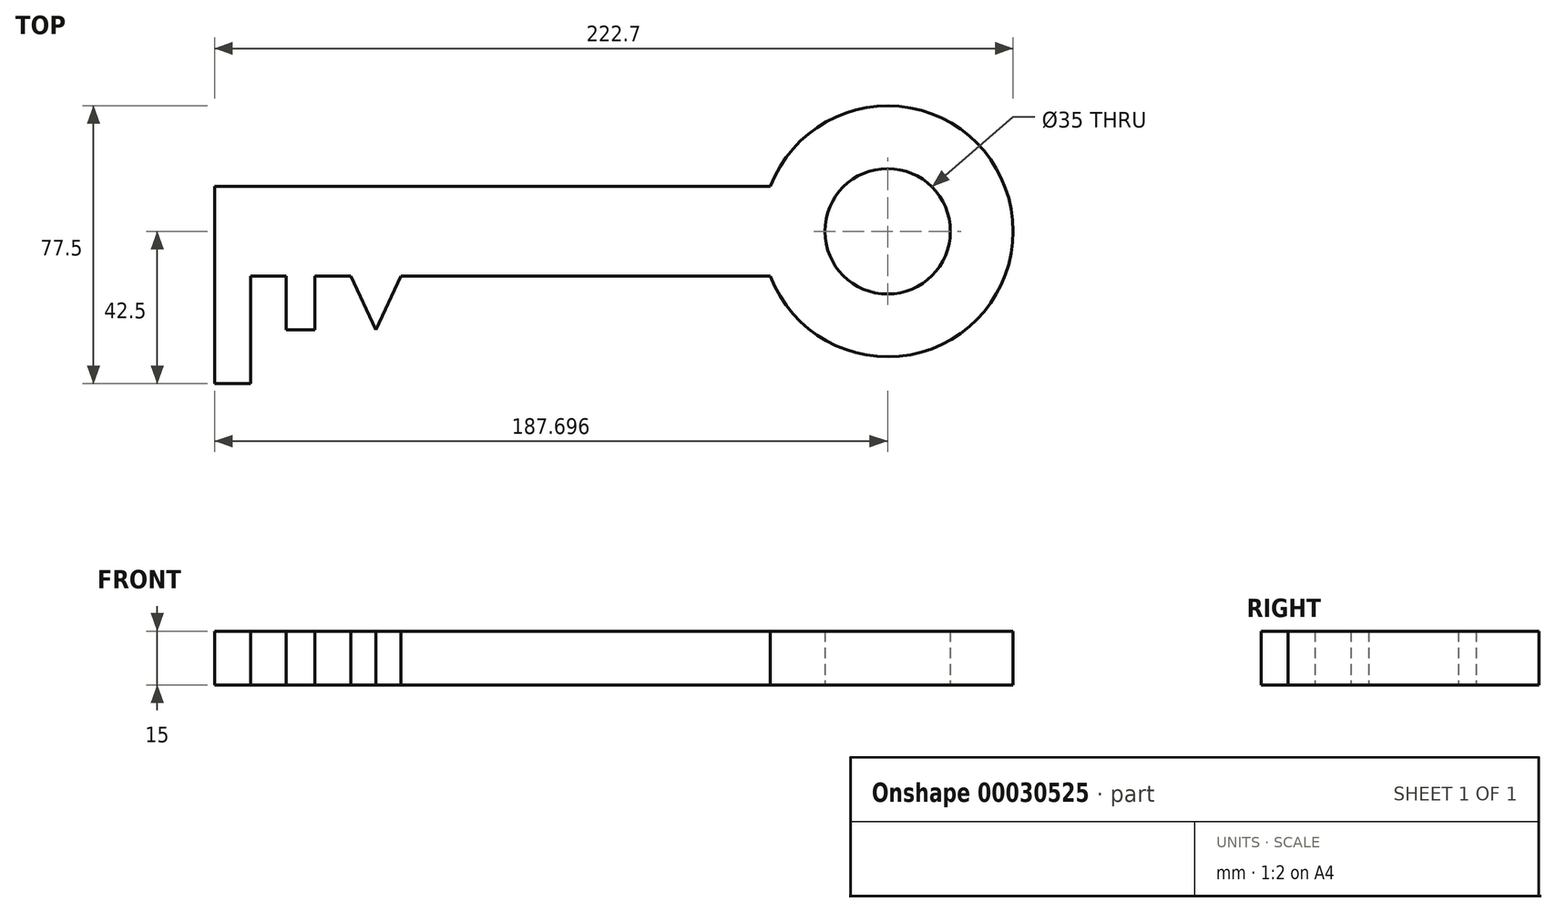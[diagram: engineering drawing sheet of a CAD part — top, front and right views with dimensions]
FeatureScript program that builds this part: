
annotation { "Feature Type Name" : "Feature", "Feature Type Description" : "" }
export const myFeature = defineFeature(function(context is Context, id is Id, definition is map)
    precondition{}
    {
        {
            var Q0;
            Q0=qCreatedBy(makeId("Top.planeOp"),FACE);
            var sketch = newSketch(context, id + "F0", { "sketchPlane" : qUnion([Q0])});
            skLineSegment(sketch, "E0.bottom", {"start": v(-75.45, 25) * mm, "end": v(79.55, 25) * mm});
            skLineSegment(sketch, "E0.top", {"start": v(-75.45, 0) * mm, "end": v(-55.45, 0) * mm});
            skLineSegment(sketch, "E0.left", {"start": v(-75.45, 25) * mm, "end": v(-75.45, 0) * mm});
            skLineSegment(sketch, "E1.top", {"start": v(-75.45, -30) * mm, "end": v(-65.45, -30) * mm});
            skLineSegment(sketch, "E1.left", {"start": v(-75.45, 0) * mm, "end": v(-75.45, -30) * mm});
            skLineSegment(sketch, "E1.right", {"start": v(-65.45, 0) * mm, "end": v(-65.45, -30) * mm});
            skLineSegment(sketch, "E2.top", {"start": v(-47.45, -15) * mm, "end": v(-55.45, -15) * mm});
            skLineSegment(sketch, "E2.left", {"start": v(-47.45, 0) * mm, "end": v(-47.45, -15) * mm});
            skLineSegment(sketch, "E2.right", {"start": v(-55.45, 0) * mm, "end": v(-55.45, -15) * mm});
            skLineSegment(sketch, "E3", {"start": v(-37.45, 0) * mm, "end": v(-30.45, -15) * mm});
            skLineSegment(sketch, "E4", {"start": v(-30.45, -15) * mm, "end": v(-23.45, 0) * mm});
            skArc(sketch, "E5", {"start": v(79.55, 0) * mm, "mid": v(147.25, 12.5) * mm, "end": v(79.55, 25) * mm});
            skCircle(sketch, "E6", {"center": v(112.25, 12.5) * mm, "radius": 17.5 * mm});
            skLineSegment(sketch, "E7", {"start": v(-75.45, 12.5) * mm, "end": v(112.25, 12.5) * mm});
            skLineSegment(sketch, "E8.trimOffspring", {"start": v(-23.45, 0) * mm, "end": v(79.55, 0) * mm});
            skLineSegment(sketch, "E9.trimOffspring", {"start": v(-47.45, 0) * mm, "end": v(-37.45, 0) * mm});
            skSolve(sketch);
        }
        {
            var Q0;
            {var subQ5=sQuery(id+"F0.wireOp",EDGE,"E0.bottom");Q0=makeQuery(id+"F0.imprint","IMPRINT",FACE,{"disambiguationData":[TD([[makeQuery(id+"F0.imprint","IMPRINT",EDGE,{"derivedFrom":subQ5}),-1.0]])]});}
            var Q1;
            Q1=makeQuery(id+"F0.imprint","IMPRINT",FACE,{"disambiguationData":[TD([[makeQuery(id+"F0.imprint","IMPRINT",EDGE,{"derivedFrom":sQuery(id+"F0.wireOp",EDGE,"E1.top")}),1.0]])]});
            extrude(context, id + "F1", {"entities" : qUnion([Q0, Q1]), "depth" : 15 * mm});
        }
    });
